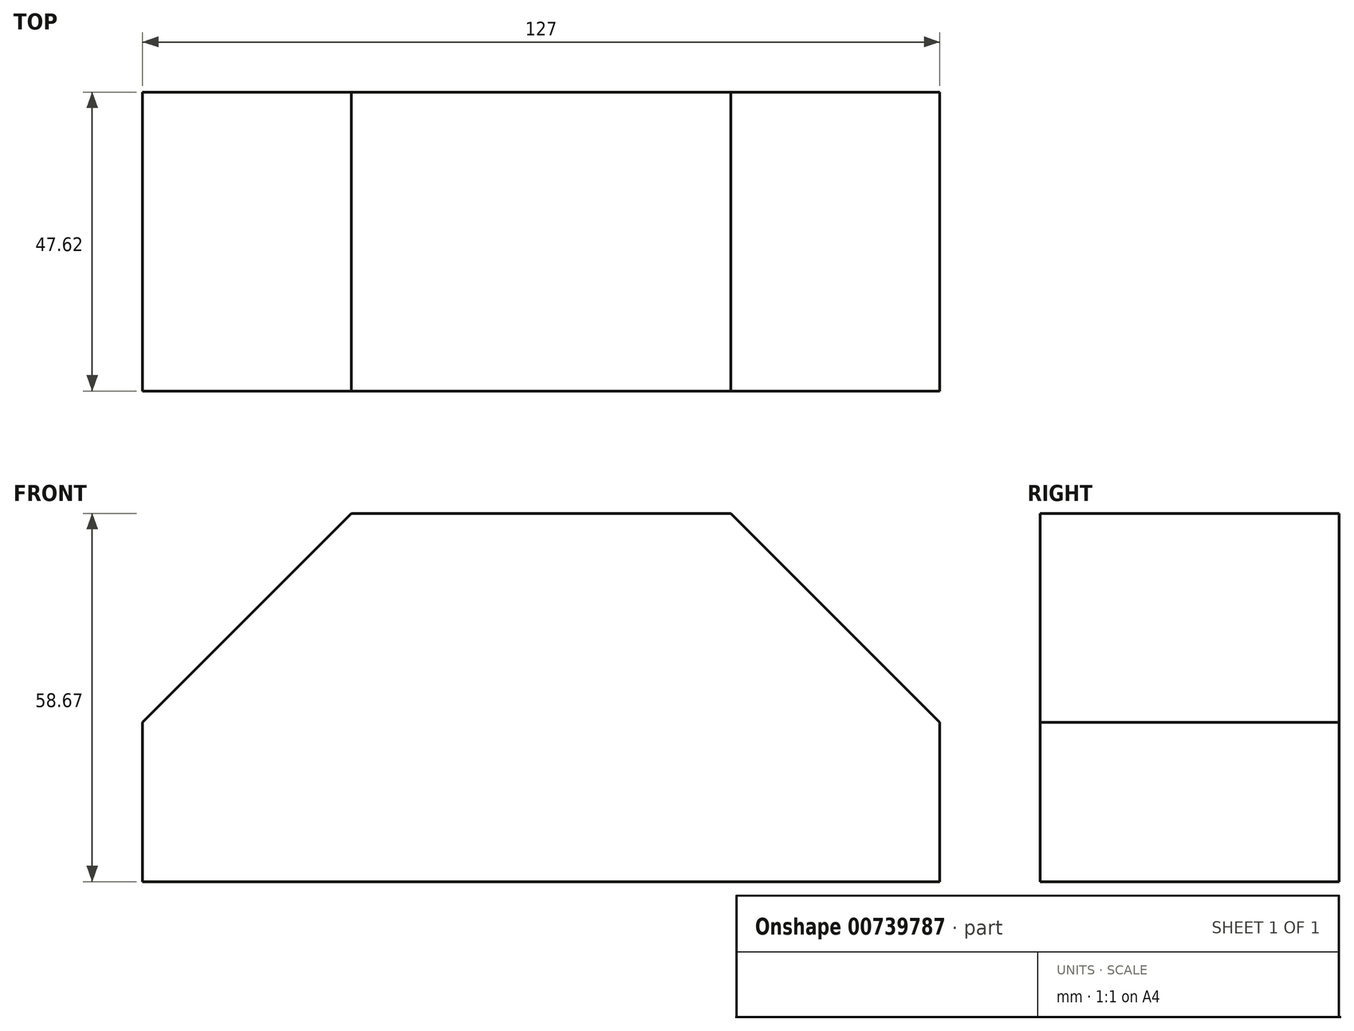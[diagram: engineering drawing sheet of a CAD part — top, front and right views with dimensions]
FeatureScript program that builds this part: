
annotation { "Feature Type Name" : "Feature", "Feature Type Description" : "" }
export const myFeature = defineFeature(function(context is Context, id is Id, definition is map)
    precondition{}
    {
        {
            var Q0;
            Q0=qCreatedBy(makeId("Front.planeOp"),FACE);
            var sketch = newSketch(context, id + "F0", { "sketchPlane" : qUnion([Q0])});
            skLineSegment(sketch, "E0", {"start": v(-70.44, 0) * mm, "end": v(-70.44, -25.4) * mm});
            skLineSegment(sketch, "E1", {"start": v(-70.44, -25.4) * mm, "end": v(56.56, -25.4) * mm});
            skLineSegment(sketch, "E2", {"start": v(56.56, -25.4) * mm, "end": v(56.56, 0) * mm});
            skLineSegment(sketch, "E3", {"start": v(56.56, 0) * mm, "end": v(23.28, 33.27) * mm});
            skLineSegment(sketch, "E4", {"start": v(23.28, 33.27) * mm, "end": v(-37.17, 33.27) * mm});
            skLineSegment(sketch, "E5", {"start": v(-37.17, 33.27) * mm, "end": v(-70.44, 0) * mm});
            skSolve(sketch);
        }
        {
            var Q0;
            Q0=makeQuery(id+"F0.imprint","IMPRINT",FACE,{"disambiguationData":[TD([[makeQuery(id+"F0.imprint","IMPRINT",EDGE,{"derivedFrom":sQuery(id+"F0.wireOp",EDGE,"E0")}),1.0]])]});
            extrude(context, id + "F1", {"entities" : qUnion([Q0]), "oppositeDirection" : true, "depth" : 47.62 * mm, "offsetDistance" : 25.4 * mm});
        }
    });
